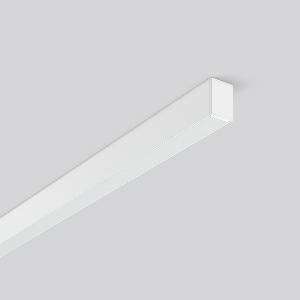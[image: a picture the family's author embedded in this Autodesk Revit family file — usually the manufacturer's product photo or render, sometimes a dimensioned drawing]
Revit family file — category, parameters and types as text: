
# Revit family: less_is_more_27_312198_002_1_9f53
name_source: partatom
category: Lighting Fixtures
units: mm (PartAtom-declared; Revit-internal decimal feet)

## family parameters
Cut with Voids When Loaded = No
Host = Face
Light Source = No
Part Type = Normal
Room Calculation Point = No
Round Connector Dimension = Use Diameter
Shared = No

## types (1)
- LESS IS MORE 27 (1 x LED Modul 840, 2350 lm, 4000)
    Apparent Load = 31 VA
    CIE Flux Codes = 48 79 96 100 100
    Color Rendering = 80
    Color Temperature = 4000
    Default Elevation = 1800 mm
    Description = Series: LESS IS MORE 27
Ceiling and wall luminaire with slim design. Housing: extruded aluminium profile, powder-coated. End cap aluminium powder-coated. Diffuser made of non-yellowing plastic (PMMA), opal. Suitable for Ceiling mounting, Wall (surface). External driver with connecting cable. 
Colour: traffic white, matt (RAL 9016)
Length: 1212 mm
Width: 28 mm
Height: 38 mm
Lamp: LED
Socket: without socket
Colour temperature: 4000K
Colour rendering index (CRI): 82
System power: 31 W
Rated luminous flux: 2350 lm
Luminous efficiency: 76 lm/W
Control gear: Regulated power supply
Protection class: II
Type of protection: IP 20
    Height = 38 mm
    Lamp = 1 x LED Modul 840
    Lamp Light Flux = 2350 lm
    Lamp count = 1
    Length = 1212 mm
    Lifetime = 50000 h
    Luminous efficacy = 76 lm/W
    Manufacturer = RZB
    ModVariant = No
    Model = 312198.002.1
    Mounting Place = Ceiling, Wall
    Mounting Type = Surface mounted
    Number of Poles = 1
    OnlyDefault = Yes
    Power Factor = 1
    Product Name = LESS IS MORE 27
    Product group = Surface mounted LED linear luminaires
    ProductGroupID = 307
    Protection Class = Protection class II
    Protection Degree = IP 20
    RLX_Detail_Level = 1
    RLX_Emergency_Light_Flux = 0 lm
    RLX_Emergency_Type = 0
    RLX_Emergency_Type_DB = No
    RlxData = <blob elided: 22809 chars, md5=e3a0f5f5>
    Socket = socket
    Standby Power = 0 W
    System Light Flux = 2350 lm
    System Power = 31 W
    Type Comments = Product without accessories
    Type Image = 312196.002.jpg
    URL = http://relux.com
    VarID = ---
    Voltage = 230 V
    Voltage Range = 220-240 V
    Weight = 0.00 kg
    Width = 28 mm

## geometry (parser evidence)
native form markers: Blend x4, Sweep x14
no freeform markers — native parametric forms only
